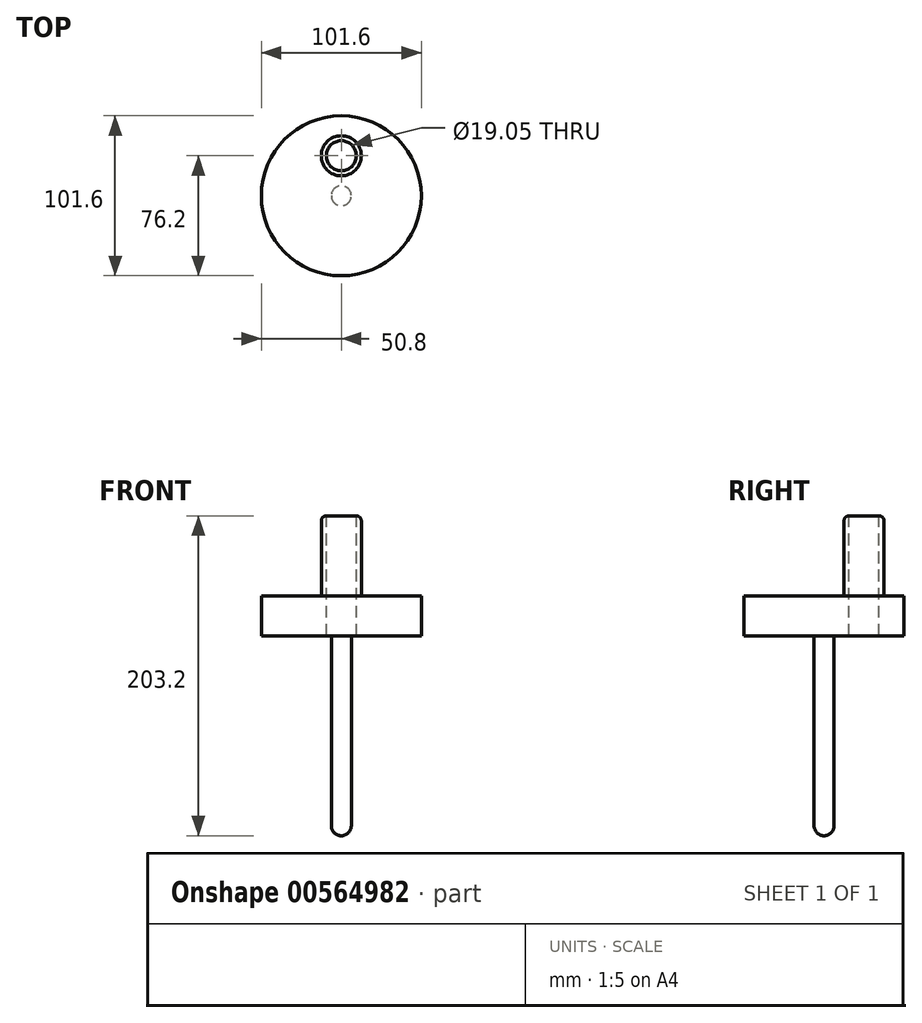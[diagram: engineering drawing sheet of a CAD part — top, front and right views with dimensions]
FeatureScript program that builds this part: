
annotation { "Feature Type Name" : "Feature", "Feature Type Description" : "" }
export const myFeature = defineFeature(function(context is Context, id is Id, definition is map)
    precondition{}
    {
        {
            var Q0;
            Q0=qCreatedBy(makeId("Top.planeOp"),FACE);
            var sketch = newSketch(context, id + "F0", { "sketchPlane" : qUnion([Q0])});
            skCircle(sketch, "E0", {"center": v(0, 0) * mm, "radius": 50.8 * mm});
            skSolve(sketch);
        }
        {
            var Q0;
            Q0 = qSketchRegion(id + "F0", true);
            extrude(context, id + "F1", {"entities" : qUnion([Q0]), "depth" : 25.4 * mm, "offsetDistance" : 25.4 * mm});
        }
        {
            var Q0;
            Q0=makeQuery(id+"F1.opExtrude","CAP_FACE",FACE,{"disambiguationData":[OSD([sQuery(id+"F0.wireOp",EDGE,"E0")])],"isStart":false});
            var sketch = newSketch(context, id + "F2", { "sketchPlane" : qUnion([Q0])});
            skCircle(sketch, "E1", {"center": v(0, 25.4) * mm, "radius": 12.7 * mm});
            skSolve(sketch);
        }
        {
            var Q0;
            Q0 = qSketchRegion(id + "F2", true);
            extrude(context, id + "F3", {"entities" : qUnion([Q0]), "operationType" : NewBodyOperationType.ADD, "depth" : 50.8 * mm, "offsetDistance" : 25.4 * mm});
        }
        {
            var Q0;
            Q0=makeQuery(id+"F3.opExtrude","CAP_FACE",FACE,{"disambiguationData":[OSD([sQuery(id+"F2.wireOp",EDGE,"E1")])],"isStart":false});
            var sketch = newSketch(context, id + "F4", { "sketchPlane" : qUnion([Q0])});
            skCircle(sketch, "E2", {"center": v(0, 25.4) * mm, "radius": 9.53 * mm});
            skSolve(sketch);
        }
        {
            var Q0;
            Q0 = qSketchRegion(id + "F4", true);
            extrude(context, id + "F5", {"entities" : qUnion([Q0]), "operationType" : NewBodyOperationType.REMOVE, "endBound" : BoundingType.THROUGH_ALL, "oppositeDirection" : true, "depth" : 25.4 * mm, "offsetDistance" : 25.4 * mm});
        }
        {
            var Q0;
            Q0=makeQuery(id+"F3.opExtrude","CAP_EDGE",EDGE,{"disambiguationData":[OSD([sQuery(id+"F2.wireOp",EDGE,"E1")])],"isStart":false});
            var Q1;
            Q1=makeQuery(id+"F3.opExtrude","CAP_EDGE",EDGE,{"disambiguationData":[OSD([sQuery(id+"F2.wireOp",EDGE,"E1")])],"isStart":true});
            fillet(context, id + "F6", {"entities" : qUnion([Q0, Q1]), "radius" : 3.17 * mm, "tangentPropagation" : true, "allowEdgeOverflow" : false});
        }
        {
            var Q0;
            Q0=makeQuery(id+"F1.opExtrude","CAP_FACE",FACE,{"disambiguationData":[OSD([sQuery(id+"F0.wireOp",EDGE,"E0")])],"isStart":true});
            var sketch = newSketch(context, id + "F7", { "sketchPlane" : qUnion([Q0])});
            skCircle(sketch, "E3", {"center": v(0, 0) * mm, "radius": 6.35 * mm});
            skSolve(sketch);
        }
        {
            var Q0;
            Q0 = qSketchRegion(id + "F7", true);
            extrude(context, id + "F8", {"entities" : qUnion([Q0]), "operationType" : NewBodyOperationType.ADD, "depth" : 127 * mm, "offsetDistance" : 25.4 * mm});
        }
        {
            var Q0;
            Q0=makeQuery(id+"F8.opExtrude","CAP_EDGE",EDGE,{"disambiguationData":[OSD([sQuery(id+"F7.wireOp",EDGE,"E3")])],"isStart":false});
            fillet(context, id + "F9", {"entities" : qUnion([Q0]), "radius" : 6.35 * mm, "tangentPropagation" : true, "allowEdgeOverflow" : false});
        }
    });
